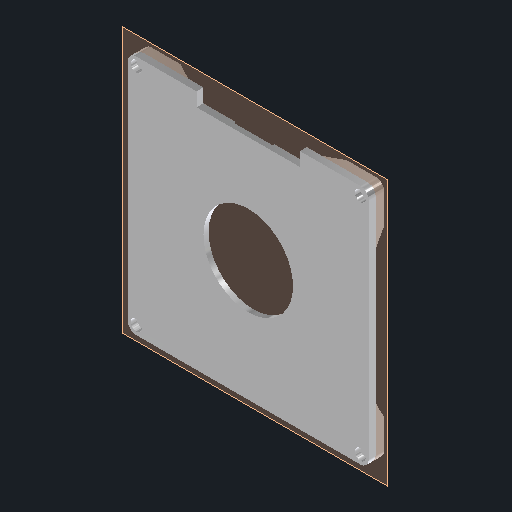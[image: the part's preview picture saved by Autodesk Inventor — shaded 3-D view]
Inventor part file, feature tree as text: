
AUTODESK INVENTOR PART (.ipt)
format: ipt  version: 2022 (Build 260153000, 153)  size: 173,056 bytes
history: native  units: mm
features: reference x12, sketch x4, other x4, plane x3, extrude x3, chamfer x1, hole x1
ambient origin geometry x8: Origin, YZ Plane, XZ Plane, XY Plane, X Axis, Y Axis, Z Axis, Center Point
bodies: Solid1 (feature_tree)
feature tree (28):
  plane  "Work Plane1"
  sketch  "Sketch1"  dims[d0=1.0mm d1=4.0mm d2=0.0mm]
  plane  "Work Plane2"
  extrude  "Extrusion1"  Depth=4.0mm TaperAngle=0.0deg
  extrude  "Extrusion2"  Depth=1.0mm TaperAngle=0.0deg
  sketch  "Sketch3"  dims[d6=4.0mm d7=0.0mm d8=5.0mm d9=2.0mm d10=45.0deg]
  plane  "Work Plane3"
  extrude  "Extrusion3"  Depth=5.0mm TaperAngle=45.0deg
  chamfer  "Chamfer1"  [1 undecoded]
  hole  "Hole1"  [1 undecoded]
  reference  "Reference1"
  reference  "Reference2"
  reference  "Reference3"
  sketch  "Sketch2"  dims[d3=2.0mm d4=1.0mm d5=0.0mm]
  reference  "Reference4"
  reference  "Reference5"
  reference  "Reference6"
  reference  "Reference7"
  reference  "Reference8"
  sketch  "Sketch4"  dims[d11=3.4mm d12=6.0mm d13=6.5mm d14=3.4mm d15=14.3117mm d16=8.8mm d17=20.594885mm]
  reference  "Reference9"
  reference  "Reference10"
  reference  "Reference11"
  reference  "Reference12"
  other  "SistemaDeElevación.iam"
  other  "soporte de rodamientos:1"
  other  "Montura de Motor:1"
  other  "BridaTornillo:1"
note: 2 required parameter values undecoded (feature->parameter linkage not recoverable at this tier; creation-order binding heuristic only, values carry confidence <= 0.55)
